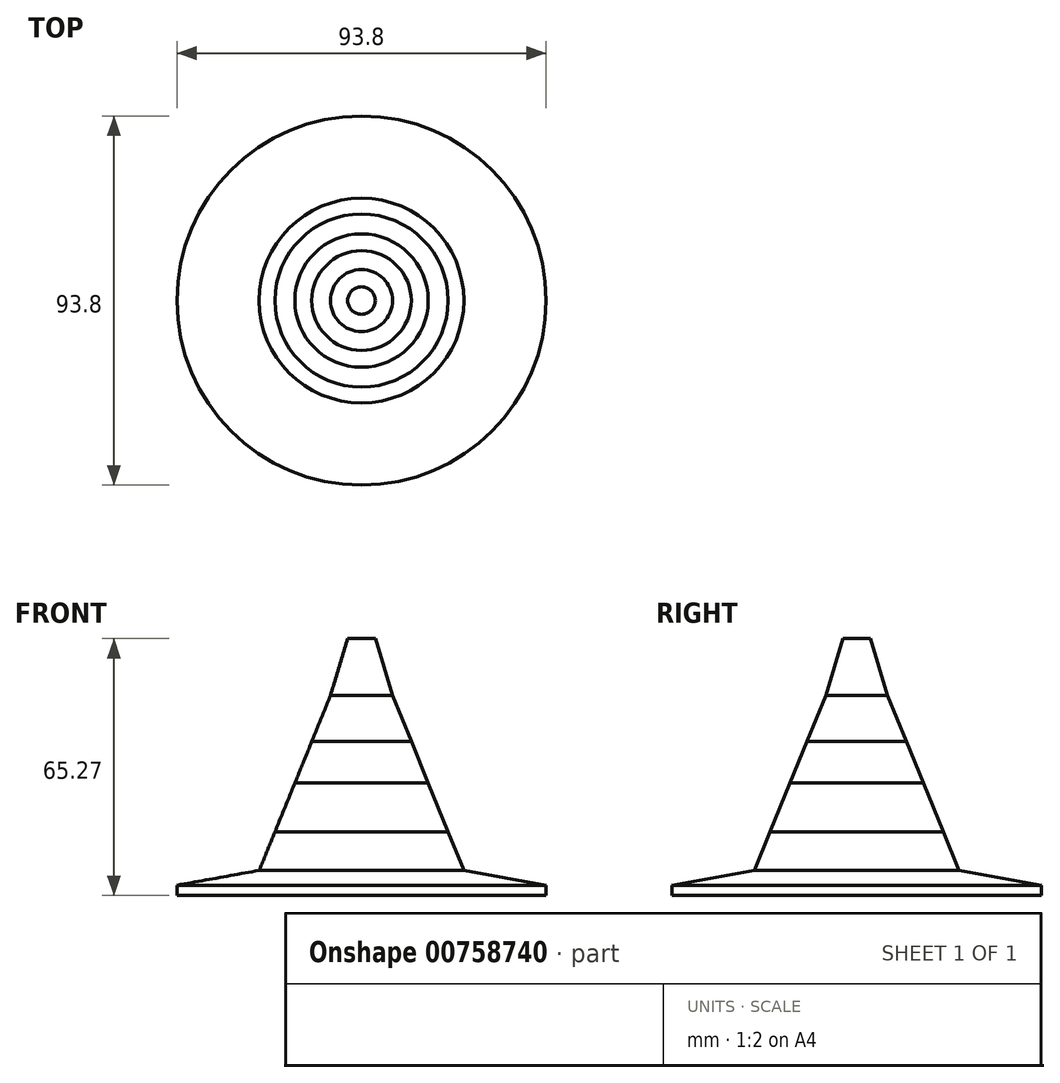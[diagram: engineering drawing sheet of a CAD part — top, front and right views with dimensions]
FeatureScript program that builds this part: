
annotation { "Feature Type Name" : "Feature", "Feature Type Description" : "" }
export const myFeature = defineFeature(function(context is Context, id is Id, definition is map)
    precondition{}
    {
        {
            var Q0;
            Q0=qCreatedBy(makeId("Front.planeOp"),FACE);
            var sketch = newSketch(context, id + "F0", { "sketchPlane" : qUnion([Q0])});
            skLineSegment(sketch, "E0", {"start": v(0, 0) * mm, "end": v(0, 50.8) * mm});
            skLineSegment(sketch, "E1", {"start": v(0, 50.8) * mm, "end": v(-7.87, 50.8) * mm});
            skLineSegment(sketch, "E2", {"start": v(-7.87, 50.8) * mm, "end": v(-26, 6.39) * mm});
            skLineSegment(sketch, "E3", {"start": v(-26, 6.39) * mm, "end": v(-46.9, 2.61) * mm});
            skLineSegment(sketch, "E4", {"start": v(-46.9, 2.61) * mm, "end": v(-46.9, 0) * mm});
            skLineSegment(sketch, "E5", {"start": v(-46.9, 0) * mm, "end": v(0, 0) * mm});
            skLineSegment(sketch, "E6", {"start": v(-12.64, 39.1) * mm, "end": v(0, 39.1) * mm});
            skLineSegment(sketch, "E7", {"start": v(-16.93, 28.6) * mm, "end": v(0, 28.6) * mm});
            skLineSegment(sketch, "E8", {"start": v(-22, 16.2) * mm, "end": v(0, 16.2) * mm});
            skLineSegment(sketch, "E9", {"start": v(0, 50.8) * mm, "end": v(0, 65.27) * mm});
            skLineSegment(sketch, "E10", {"start": v(0, 65.27) * mm, "end": v(-3.5, 65.27) * mm});
            skLineSegment(sketch, "E11", {"start": v(-3.5, 65.27) * mm, "end": v(-7.87, 50.8) * mm});
            skLineSegment(sketch, "E12", {"start": v(-5.17, 59.37) * mm, "end": v(0, 59.37) * mm});
            skSolve(sketch);
        }
        {
            var Q0;
            {var subQ0=sQuery(id+"F0.wireOp",EDGE,"E1");Q0=makeQuery(id+"F0.imprint","IMPRINT",FACE,{"disambiguationData":[TD([[makeQuery(id+"F0.imprint","IMPRINT",EDGE,{"derivedFrom":subQ0}),1.0]])]});}
            var Q1;
            Q1=sQuery(id+"F0.wireOp",EDGE,"E0");
            revolve(context, id + "F1", {"surfaceOperationType" : NewSurfaceOperationType.NEW, "entities" : qUnion([Q0]), "axis" : qUnion([Q1]), "revolveType" : RevolveType.FULL});
        }
        {
            var Q0;
            {var subQ0=sQuery(id+"F0.wireOp",EDGE,"E6");Q0=makeQuery(id+"F0.imprint","IMPRINT",FACE,{"disambiguationData":[TD([[makeQuery(id+"F0.imprint","IMPRINT",EDGE,{"derivedFrom":subQ0}),-1.0]])]});}
            var Q1;
            Q1=sQuery(id+"F0.wireOp",EDGE,"E0");
            revolve(context, id + "F2", {"surfaceOperationType" : NewSurfaceOperationType.NEW, "entities" : qUnion([Q0]), "axis" : qUnion([Q1]), "revolveType" : RevolveType.FULL});
        }
        {
            var Q0;
            {var subQ0=sQuery(id+"F0.wireOp",EDGE,"E7");Q0=makeQuery(id+"F0.imprint","IMPRINT",FACE,{"disambiguationData":[TD([[makeQuery(id+"F0.imprint","IMPRINT",EDGE,{"derivedFrom":subQ0}),-1.0]])]});}
            var Q1;
            Q1=sQuery(id+"F0.wireOp",EDGE,"E0");
            revolve(context, id + "F3", {"surfaceOperationType" : NewSurfaceOperationType.NEW, "entities" : qUnion([Q0]), "axis" : qUnion([Q1]), "revolveType" : RevolveType.FULL});
        }
        {
            var Q0;
            {var subQ0=sQuery(id+"F0.wireOp",EDGE,"E3");Q0=makeQuery(id+"F0.imprint","IMPRINT",FACE,{"disambiguationData":[TD([[makeQuery(id+"F0.imprint","IMPRINT",EDGE,{"derivedFrom":subQ0}),1.0]])]});}
            var Q1;
            Q1=sQuery(id+"F0.wireOp",EDGE,"E0");
            revolve(context, id + "F4", {"surfaceOperationType" : NewSurfaceOperationType.NEW, "entities" : qUnion([Q0]), "axis" : qUnion([Q1]), "revolveType" : RevolveType.FULL});
        }
        {
            var Q0;
            {var subQ3=sQuery(id+"F0.wireOp",EDGE,"E1");Q0=makeQuery(id+"F0.imprint","IMPRINT",FACE,{"disambiguationData":[TD([[makeQuery(id+"F0.imprint","IMPRINT",EDGE,{"derivedFrom":subQ3}),-1.0]])]});}
            var Q1;
            Q1=sQuery(id+"F0.wireOp",EDGE,"E9");
            revolve(context, id + "F5", {"surfaceOperationType" : NewSurfaceOperationType.NEW, "entities" : qUnion([Q0]), "axis" : qUnion([Q1]), "revolveType" : RevolveType.FULL});
        }
    });
